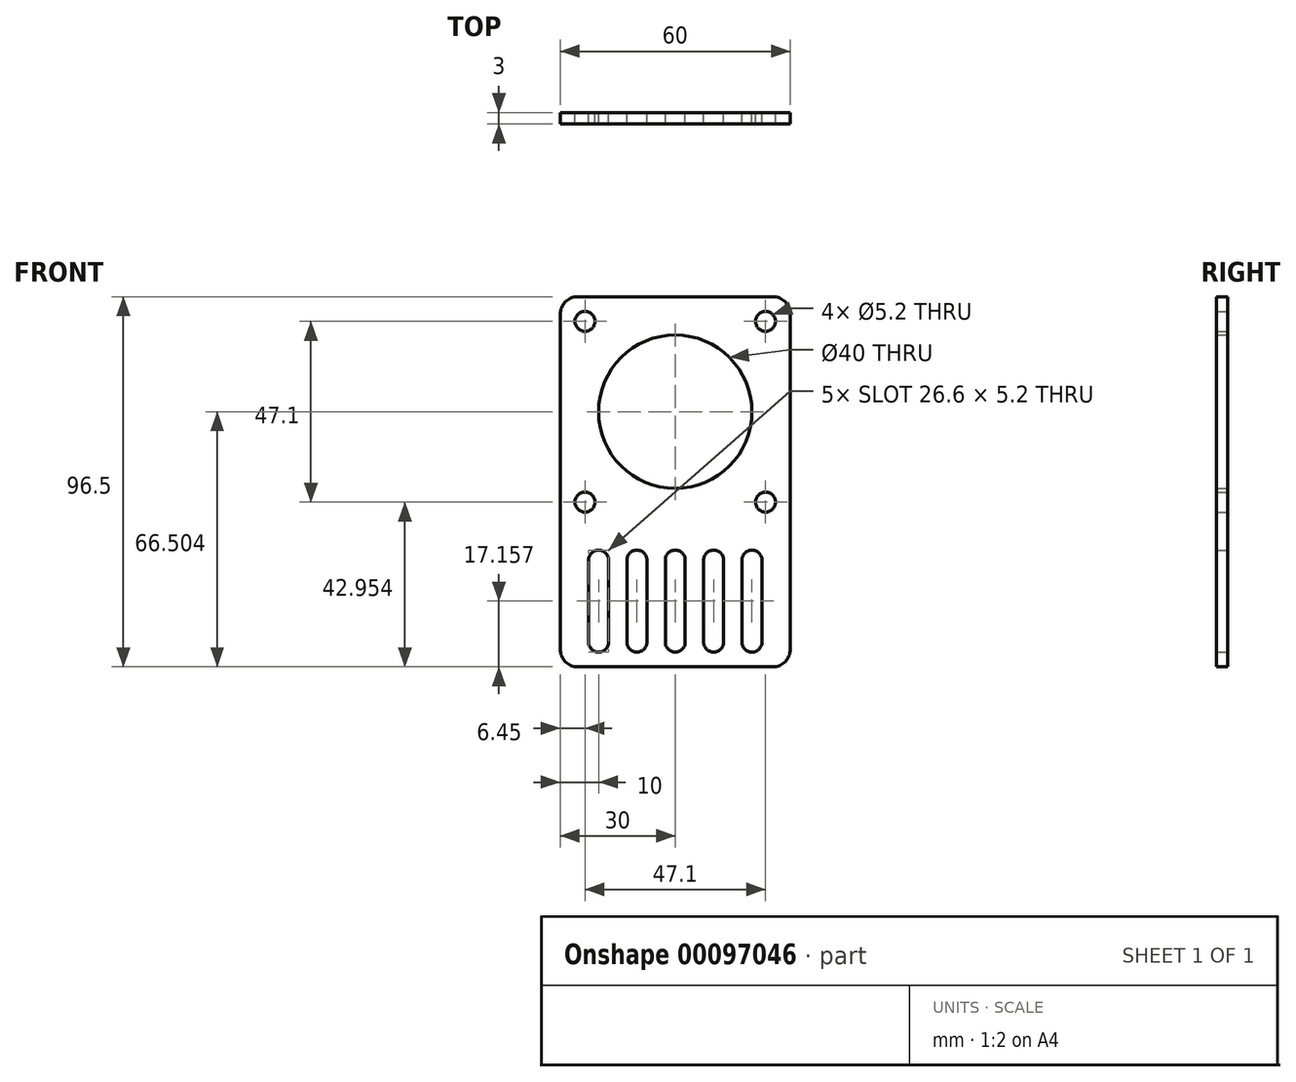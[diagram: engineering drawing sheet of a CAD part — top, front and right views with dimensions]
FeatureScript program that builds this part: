
annotation { "Feature Type Name" : "Feature", "Feature Type Description" : "" }
export const myFeature = defineFeature(function(context is Context, id is Id, definition is map)
    precondition{}
    {
        {
            var Q0;
            Q0=qCreatedBy(makeId("Front.planeOp"),FACE);
            var sketch = newSketch(context, id + "F0", { "sketchPlane" : qUnion([Q0])});
            skLineSegment(sketch, "E0.bottom", {"start": v(-25.4, -41.19) * mm, "end": v(25.4, -41.19) * mm});
            skLineSegment(sketch, "E0.top", {"start": v(-25.4, 55.31) * mm, "end": v(25.4, 55.31) * mm});
            skLineSegment(sketch, "E0.left", {"start": v(-30, -36.59) * mm, "end": v(-30, 50.71) * mm});
            skLineSegment(sketch, "E0.right", {"start": v(30, -36.59) * mm, "end": v(30, 50.71) * mm});
            skLineSegment(sketch, "E1", {"start": v(0, 55.31) * mm, "end": v(0, -41.19) * mm, "construction": true});
            skArc(sketch, "E2", {"start": v(2.6, -13.33) * mm, "mid": v(0, -10.73) * mm, "end": v(-2.6, -13.33) * mm});
            skArc(sketch, "E3", {"start": v(-2.6, -34.73) * mm, "mid": v(0, -37.33) * mm, "end": v(2.6, -34.73) * mm});
            skLineSegment(sketch, "E4", {"start": v(2.6, -13.33) * mm, "end": v(2.6, -34.73) * mm});
            skLineSegment(sketch, "E5", {"start": v(-2.6, -13.33) * mm, "end": v(-2.6, -34.73) * mm});
            skArc(sketch, "E6.1.0.0", {"start": v(12.6, -13.33) * mm, "mid": v(10, -10.73) * mm, "end": v(7.4, -13.33) * mm});
            skArc(sketch, "E6.1.0.1", {"start": v(7.4, -34.73) * mm, "mid": v(10, -37.33) * mm, "end": v(12.6, -34.73) * mm});
            skLineSegment(sketch, "E6.1.0.2", {"start": v(12.6, -13.33) * mm, "end": v(12.6, -34.73) * mm});
            skLineSegment(sketch, "E6.1.0.3", {"start": v(7.4, -13.33) * mm, "end": v(7.4, -34.73) * mm});
            skArc(sketch, "E6.2.0.0", {"start": v(22.6, -13.33) * mm, "mid": v(20, -10.73) * mm, "end": v(17.4, -13.33) * mm});
            skArc(sketch, "E6.2.0.1", {"start": v(17.4, -34.73) * mm, "mid": v(20, -37.33) * mm, "end": v(22.6, -34.73) * mm});
            skLineSegment(sketch, "E6.2.0.2", {"start": v(22.6, -13.33) * mm, "end": v(22.6, -34.73) * mm});
            skLineSegment(sketch, "E6.2.0.3", {"start": v(17.4, -13.33) * mm, "end": v(17.4, -34.73) * mm});
            skLineSegment(sketch, "E6.direction1", {"start": v(-2.6, -13.33) * mm, "end": v(7.4, -13.33) * mm, "construction": true});
            skArc(sketch, "E7.1.0.0", {"start": v(-7.4, -13.33) * mm, "mid": v(-10, -10.73) * mm, "end": v(-12.6, -13.33) * mm});
            skArc(sketch, "E7.1.0.1", {"start": v(-12.6, -34.73) * mm, "mid": v(-10, -37.33) * mm, "end": v(-7.4, -34.73) * mm});
            skLineSegment(sketch, "E7.1.0.2", {"start": v(-7.4, -13.33) * mm, "end": v(-7.4, -34.73) * mm});
            skLineSegment(sketch, "E7.1.0.3", {"start": v(-12.6, -13.33) * mm, "end": v(-12.6, -34.73) * mm});
            skArc(sketch, "E7.2.0.0", {"start": v(-17.4, -13.33) * mm, "mid": v(-20, -10.73) * mm, "end": v(-22.6, -13.33) * mm});
            skArc(sketch, "E7.2.0.1", {"start": v(-22.6, -34.73) * mm, "mid": v(-20, -37.33) * mm, "end": v(-17.4, -34.73) * mm});
            skLineSegment(sketch, "E7.2.0.2", {"start": v(-17.4, -13.33) * mm, "end": v(-17.4, -34.73) * mm});
            skLineSegment(sketch, "E7.2.0.3", {"start": v(-22.6, -13.33) * mm, "end": v(-22.6, -34.73) * mm});
            skLineSegment(sketch, "E7.direction1", {"start": v(-2.6, -13.33) * mm, "end": v(-12.6, -13.33) * mm, "construction": true});
            skLineSegment(sketch, "E8", {"start": v(-30, 55.31) * mm, "end": v(30, -4.69) * mm, "construction": true});
            skLineSegment(sketch, "E9", {"start": v(30, 55.31) * mm, "end": v(-30, -4.69) * mm, "construction": true});
            skCircle(sketch, "E10", {"center": v(23.55, 48.86) * mm, "radius": 2.6 * mm});
            skCircle(sketch, "E11", {"center": v(-23.55, 48.86) * mm, "radius": 2.6 * mm});
            skCircle(sketch, "E12", {"center": v(23.55, 1.76) * mm, "radius": 2.6 * mm});
            skCircle(sketch, "E13", {"center": v(-23.55, 1.76) * mm, "radius": 2.6 * mm});
            skCircle(sketch, "E14", {"center": v(0, 25.31) * mm, "radius": 20 * mm});
            skPoint(sketch, "E15.visualSharp", {"position": v(30, 55.31) * mm});
            skArc(sketch, "E15.filletArc", {"start": v(30, 50.71) * mm, "mid": v(28.65, 53.97) * mm, "end": v(25.4, 55.31) * mm});
            skPoint(sketch, "E16.visualSharp", {"position": v(30, -41.19) * mm});
            skArc(sketch, "E16.filletArc", {"start": v(25.4, -41.19) * mm, "mid": v(28.65, -39.84) * mm, "end": v(30, -36.59) * mm});
            skPoint(sketch, "E17.visualSharp", {"position": v(-30, -41.19) * mm});
            skArc(sketch, "E17.filletArc", {"start": v(-30, -36.59) * mm, "mid": v(-28.65, -39.84) * mm, "end": v(-25.4, -41.19) * mm});
            skPoint(sketch, "E18.visualSharp", {"position": v(-30, 55.31) * mm});
            skArc(sketch, "E18.filletArc", {"start": v(-25.4, 55.31) * mm, "mid": v(-28.65, 53.97) * mm, "end": v(-30, 50.71) * mm});
            skSolve(sketch);
        }
        {
            var Q0;
            Q0=qSketchRegion(id+"F0",true);
            extrude(context, id + "F1", {"entities" : qUnion([Q0]), "depth" : 3 * mm});
        }
    });
